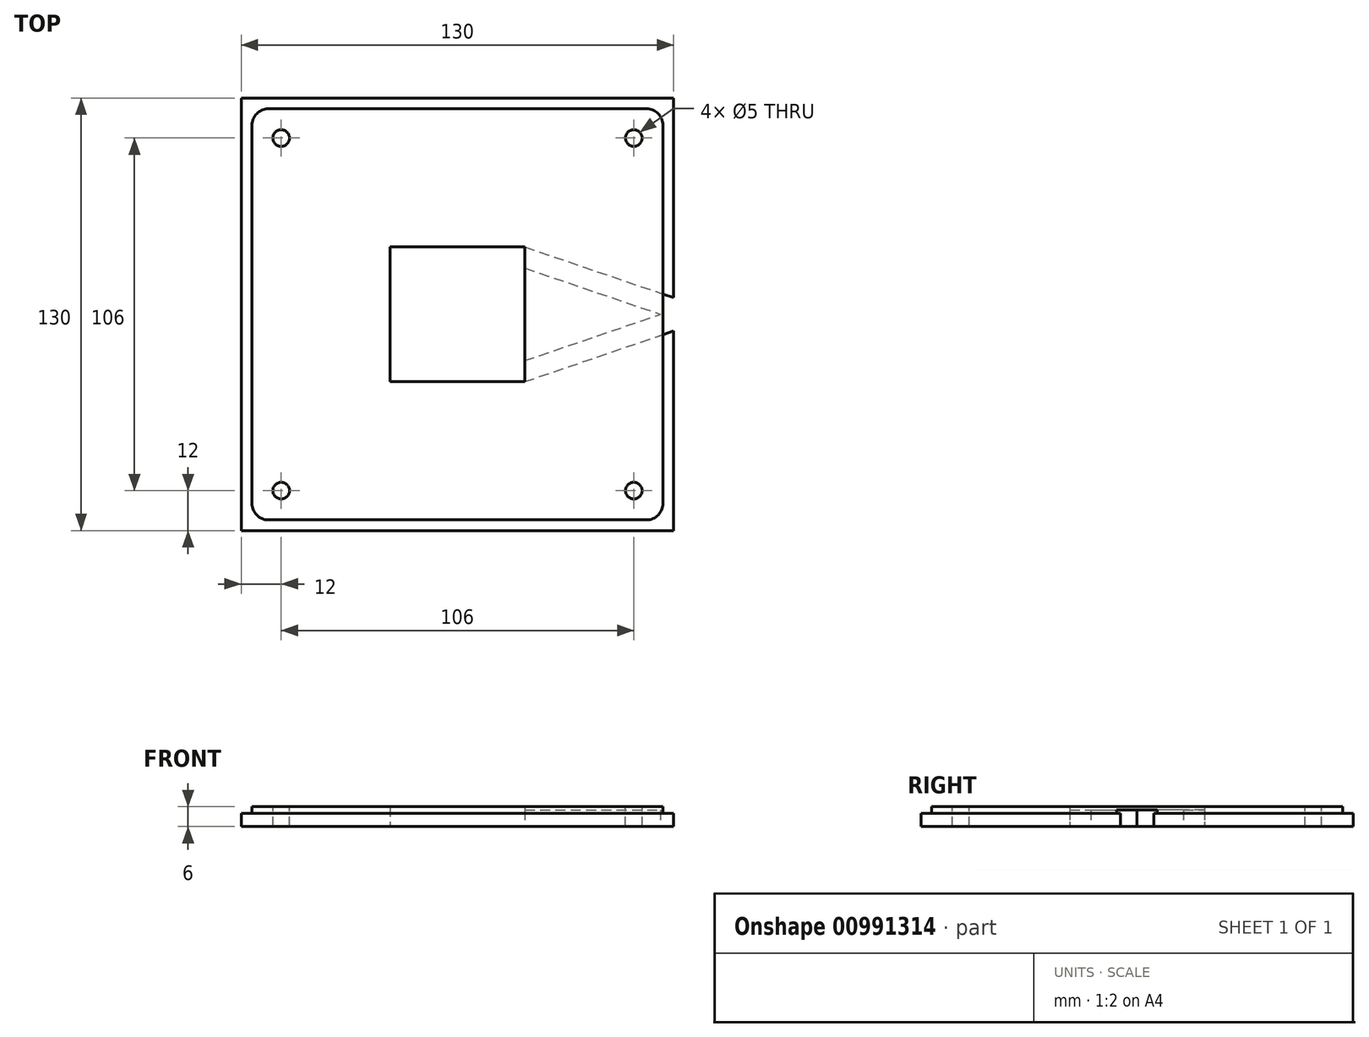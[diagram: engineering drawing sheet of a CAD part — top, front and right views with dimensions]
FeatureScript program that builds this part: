
annotation { "Feature Type Name" : "Feature", "Feature Type Description" : "" }
export const myFeature = defineFeature(function(context is Context, id is Id, definition is map)
    precondition{}
    {
        {
            var Q0;
            Q0=qCreatedBy(makeId("Top.planeOp"),FACE);
            var sketch = newSketch(context, id + "F0", { "sketchPlane" : qUnion([Q0])});
            skLineSegment(sketch, "E0.bottom", {"start": v(-53, 53) * mm, "end": v(53, 53) * mm, "construction": true});
            skLineSegment(sketch, "E0.top", {"start": v(-53, -53) * mm, "end": v(53, -53) * mm, "construction": true});
            skLineSegment(sketch, "E0.left", {"start": v(-53, 53) * mm, "end": v(-53, -53) * mm, "construction": true});
            skLineSegment(sketch, "E0.right", {"start": v(53, 53) * mm, "end": v(53, -53) * mm, "construction": true});
            skPoint(sketch, "E0.middle", {"position": v(0, 0) * mm});
            skLineSegment(sketch, "E1.bottom", {"start": v(-65, 65) * mm, "end": v(65, 65) * mm});
            skLineSegment(sketch, "E1.top", {"start": v(-65, -65) * mm, "end": v(65, -65) * mm});
            skLineSegment(sketch, "E1.left", {"start": v(-65, 65) * mm, "end": v(-65, -65) * mm});
            skLineSegment(sketch, "E1.right", {"start": v(65, 65) * mm, "end": v(65, -65) * mm});
            skSolve(sketch);
        }
        {
            var Q0;
            Q0 = qSketchRegion(id + "F0", true);
            extrude(context, id + "F1", {"entities" : qUnion([Q0]), "depth" : 4 * mm, "offsetDistance" : 25 * mm});
        }
        {
            var Q0;
            Q0=sQuery(id+"F0.wireOp",VERTEX,"E0.bottom.start");
            var Q1;
            Q1=sQuery(id+"F0.wireOp",VERTEX,"E0.bottom.end");
            var Q2;
            Q2=sQuery(id+"F0.wireOp",VERTEX,"E0.top.start");
            var Q3;
            Q3=sQuery(id+"F0.wireOp",VERTEX,"E0.top.end");
            var Q4;
            Q4=makeQuery(id+"F1.opExtrude","SWEPT_BODY",BODY,{"disambiguationData":[OSD([sQuery(id+"F0.wireOp",EDGE,"E1.bottom"),sQuery(id+"F0.wireOp",EDGE,"E1.top"),sQuery(id+"F0.wireOp",EDGE,"E1.left"),sQuery(id+"F0.wireOp",EDGE,"E1.right")])]});
            hole(context, id + "F2", {"style" : HoleStyle.SIMPLE, "endStyle" : HoleEndStyle.BLIND, "oppositeDirection" : true, "holeDiameter" : 5 * mm, "majorDiameter" : 5 * mm, "holeDepth" : 4 * mm, "isTappedThrough" : true, "tappedDepth" : 12 * mm, "tapClearance" : 3, "locations" : qUnion([Q0, Q1, Q2, Q3]), "scope" : qUnion([Q4]), "startStyle" : HoleStartStyle.PART});
        }
        {
            var Q0;
            Q0=makeQuery(id+"F1.opExtrude","CAP_FACE",FACE,{"disambiguationData":[OSD([sQuery(id+"F0.wireOp",EDGE,"E1.bottom"),sQuery(id+"F0.wireOp",EDGE,"E1.top"),sQuery(id+"F0.wireOp",EDGE,"E1.left"),sQuery(id+"F0.wireOp",EDGE,"E1.right")])],"isStart":false});
            var sketch = newSketch(context, id + "F3", { "sketchPlane" : qUnion([Q0])});
            skLineSegment(sketch, "E2.0", {"start": v(-61.8, 61.8) * mm, "end": v(61.8, 61.8) * mm});
            skLineSegment(sketch, "E2.1", {"start": v(-61.8, 61.8) * mm, "end": v(-61.8, -61.8) * mm});
            skLineSegment(sketch, "E2.2", {"start": v(-61.8, -61.8) * mm, "end": v(61.8, -61.8) * mm});
            skLineSegment(sketch, "E2.3", {"start": v(61.8, 61.8) * mm, "end": v(61.8, -61.8) * mm});
            skSolve(sketch);
        }
        {
            var Q0;
            Q0=makeQuery(id+"F3.imprint","IMPRINT",FACE,{"disambiguationData":[TD([[makeQuery(id+"F3.imprint","IMPRINT",EDGE,{"derivedFrom":sQuery(id+"F3.wireOp",EDGE,"E2.0")}),-1.0]])]});
            extrude(context, id + "F4", {"entities" : qUnion([Q0]), "operationType" : NewBodyOperationType.ADD, "depth" : 2 * mm, "offsetDistance" : 25 * mm});
        }
        {
            var Q0;
            Q0=makeQuery(id+"F4.opExtrude","SWEPT_EDGE",EDGE,{"disambiguationData":[OSD([sQuery(id+"F3.wireOp",EDGE,"E2.2"),sQuery(id+"F3.wireOp",EDGE,"E2.3")])]});
            var Q1;
            Q1=makeQuery(id+"F4.opExtrude","SWEPT_EDGE",EDGE,{"disambiguationData":[OSD([sQuery(id+"F3.wireOp",EDGE,"E2.1"),sQuery(id+"F3.wireOp",EDGE,"E2.2")])]});
            var Q2;
            Q2=makeQuery(id+"F4.opExtrude","SWEPT_EDGE",EDGE,{"disambiguationData":[OSD([sQuery(id+"F3.wireOp",EDGE,"E2.0"),sQuery(id+"F3.wireOp",EDGE,"E2.1")])]});
            var Q3;
            Q3=makeQuery(id+"F4.opExtrude","SWEPT_EDGE",EDGE,{"disambiguationData":[OSD([sQuery(id+"F3.wireOp",EDGE,"E2.0"),sQuery(id+"F3.wireOp",EDGE,"E2.3")])]});
            fillet(context, id + "F5", {"entities" : qUnion([Q0, Q1, Q2, Q3]), "radius" : 5 * mm, "tangentPropagation" : true, "defaultsChanged" : true, "vertexSettings" : [], "allowEdgeOverflow" : false});
        }
        {
            var Q0;
            Q0=makeQuery(id+"F0.imprint","IMPRINT",FACE,{"disambiguationData":[TD([[makeQuery(id+"F0.imprint","IMPRINT",EDGE,{"derivedFrom":sQuery(id+"F0.wireOp",EDGE,"E1.bottom")}),-1.0]])]});
            var sketch = newSketch(context, id + "F6", { "sketchPlane" : qUnion([Q0])});
            skLineSegment(sketch, "E3.bottom", {"start": v(-20.25, -20.25) * mm, "end": v(20.25, -20.25) * mm});
            skLineSegment(sketch, "E3.top", {"start": v(-20.25, 20.25) * mm, "end": v(20.25, 20.25) * mm});
            skLineSegment(sketch, "E3.left", {"start": v(-20.25, -20.25) * mm, "end": v(-20.25, 20.25) * mm});
            skLineSegment(sketch, "E3.right", {"start": v(20.25, -20.25) * mm, "end": v(20.25, 20.25) * mm});
            skPoint(sketch, "E3.middle", {"position": v(0, 0) * mm});
            skLineSegment(sketch, "E4", {"start": v(20.25, -20.25) * mm, "end": v(65, -5) * mm});
            skLineSegment(sketch, "E5", {"start": v(20.25, 20.25) * mm, "end": v(65, 5) * mm});
            skLineSegment(sketch, "E6", {"start": v(65, -5) * mm, "end": v(65, 5) * mm});
            skLineSegment(sketch, "E7", {"start": v(20.25, -13.91) * mm, "end": v(61.07, 0) * mm});
            skLineSegment(sketch, "E8", {"start": v(20.25, 13.91) * mm, "end": v(63.06, -0.68) * mm});
            skSolve(sketch);
        }
        {
            var Q0;
            Q0=makeQuery(id+"F6.imprint","IMPRINT",FACE,{"disambiguationData":[TD([[makeQuery(id+"F6.imprint","IMPRINT",EDGE,{"derivedFrom":sQuery(id+"F6.wireOp",EDGE,"E3.bottom")}),1.0]])]});
            extrude(context, id + "F7", {"entities" : qUnion([Q0]), "operationType" : NewBodyOperationType.REMOVE, "depth" : 6 * mm, "offsetDistance" : 25 * mm});
        }
        {
            var Q0;
            Q0=makeQuery(id+"F6.imprint","IMPRINT",FACE,{"disambiguationData":[TD([[makeQuery(id+"F6.imprint","IMPRINT",EDGE,{"derivedFrom":sQuery(id+"F6.wireOp",EDGE,"E3.right")}),-1.0]])]});
            extrude(context, id + "F8", {"entities" : qUnion([Q0]), "operationType" : NewBodyOperationType.REMOVE, "depth" : 5 * mm, "offsetDistance" : 25 * mm});
        }
    });
